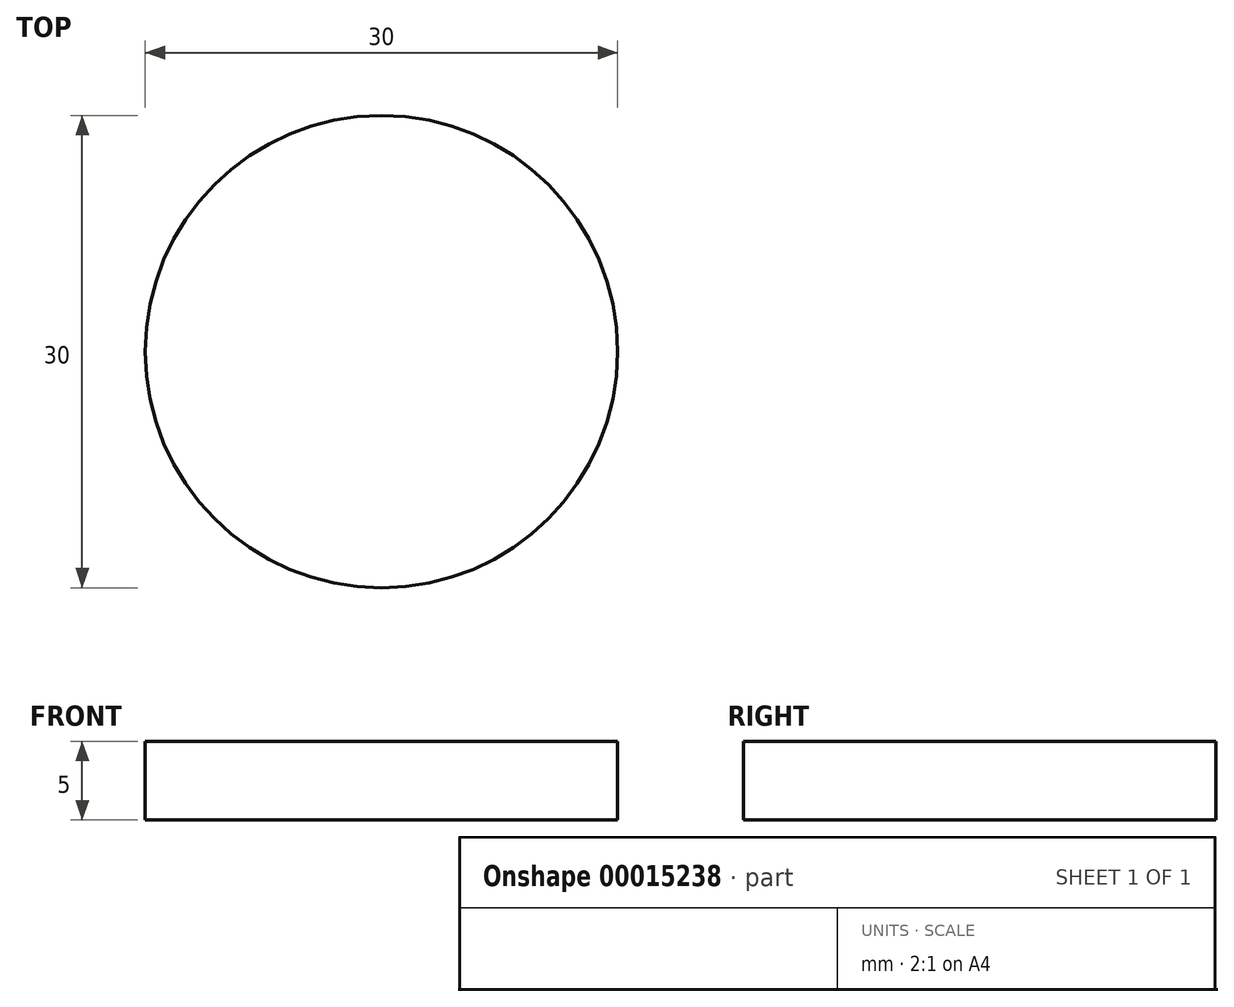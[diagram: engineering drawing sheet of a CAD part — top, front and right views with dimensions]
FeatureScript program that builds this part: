
annotation { "Feature Type Name" : "Feature", "Feature Type Description" : "" }
export const myFeature = defineFeature(function(context is Context, id is Id, definition is map)
    precondition{}
    {
        {
            var Q0;
            Q0=qCreatedBy(makeId("Top.planeOp"),FACE);
            var sketch = newSketch(context, id + "F0", { "sketchPlane" : qUnion([Q0])});
            skCircle(sketch, "E0", {"center": v(0, 0) * mm, "radius": 15 * mm});
            skSolve(sketch);
        }
        {
            var Q0;
            Q0=sQuery(id+"F0.wireOp",EDGE,"E0");
            extrude(context, id + "F1", {"bodyType" : ToolBodyType.SURFACE, "surfaceEntities" : qUnion([Q0]), "depth" : 5 * mm});
        }
    });
